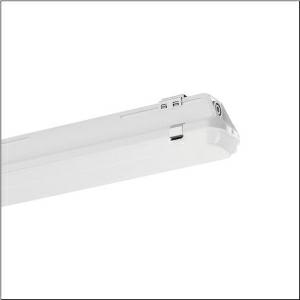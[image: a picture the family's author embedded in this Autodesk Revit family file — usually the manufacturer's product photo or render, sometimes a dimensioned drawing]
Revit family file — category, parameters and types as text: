
# Revit family: monsun_r__11_emergency_51fp20dp467l3h_369f
name_source: partatom
category: Lighting Fixtures
units: mm (PartAtom-declared; Revit-internal decimal feet)

## family parameters
Cut with Voids When Loaded = No
Host = Face
Light Source = No
Part Type = Normal
Room Calculation Point = No
Round Connector Dimension = Use Diameter
Shared = No

## types (1)
- --- (1 x LED, 910 lm, 6.2 W, 4000K)
    Apparent Load = 6 VA
    CIE Flux Codes = 45 75 93 94 100
    Color Rendering = 80
    Color Temperature = 4000K
    Default Elevation = 1800 mm
    Description = Monsun® 11 emergency, damp-proof luminaire, chain hanger, primary optical cover: enclosure, of PC, light emission: direct distribution, primary light characteristic: symmetric, installation type: suspended mounting, surface-mounted, horizontal mounting, vertical mounting, LED, rated luminous flux: 5.450lm, luminous efficacy: 173lm/W, light colour: 840, colour temperature: 4000K, control gear: DALI 2, with terminal, 5+3-pole, max. 2.5mm², mains connection: 220..240V, AC, 50/60Hz, rated input power: 35W, control gear: single battery element, battery: LiFePO4, 9Ah, luminaire housing, of glass-fibre reinforced polyester, uncoated, bright grey, incl. chain hanger, length: 1.590mm, width: 90mm, height: 88mm, clip for enclosure, of stainless steel (V2A), ceiling mounting element, of stainless steel (V2A), chain hanger, of stainless steel (V2A), protection rating (complete): IP66, insulation class (complete): insulation class I (protective earthing), certification: CE, UKCA, protection symbol: D, impact resistance: IK08, permissible operating ambient temperature: +5..+35°C, standard: EN 50419, EN 60598-2-1, EN 60598-2-22, contact your sales advisor before using the luminaires in applications with unclear chemical exposure, large temperature fluctuations or condensation-forming humidity, LABS conformity tested according to VDMA 24364:2018-05, no direct snow, no direct sun, no direct rain, for indoor or canopied outdoor use, corresponds to IFS (International Featured Standards) requirements for safety and quality in the food industry, packaging unit: 1 piece
    Height = 89 mm
    Lamp = 1 x LED
    Lamp Light Flux = 910 lm
    Lamp Power = 6.2 W
    Lamp count = 1
    Length = 1590 mm
    Luminous efficacy = 147 lm/W
    Manufacturer = Siteco
    ModVariant = No
    Model = 51FP20DP467L3H
    Mounting Place = Ceiling
    Mounting Type = Surface mounted
    Number of Poles = 1
    OnlyDefault = Yes
    Power Factor = 1
    Product Name = Monsun® 11 emergency
    Product group = damp-proof luminaire
    ProductGroupID = 300
    Protection Class = Protection class I
    Protection Degree = IP 66
    RLX_Detail_Level = 1
    RLX_Emergency_Light_Flux = 0 lm
    RLX_Emergency_Type = 0
    RLX_Emergency_Type_DB = No
    RlxData = <blob elided: 92329 chars, md5=22ac8095>
    Socket = socket
    Standby Power = 0 W
    System Light Flux = 910 lm
    System Power = 6 W
    Type Comments = : emergency light operation: 3 h
    Type Image = l_1349237.jpg
    URL = http://relux.com
    VarID = @adj_018226
    Voltage = 0 V
    Weight = 0.00 kg
    Width = 90 mm

## geometry (parser evidence)
native form markers: Blend x4, Sweep x14
no freeform markers — native parametric forms only
